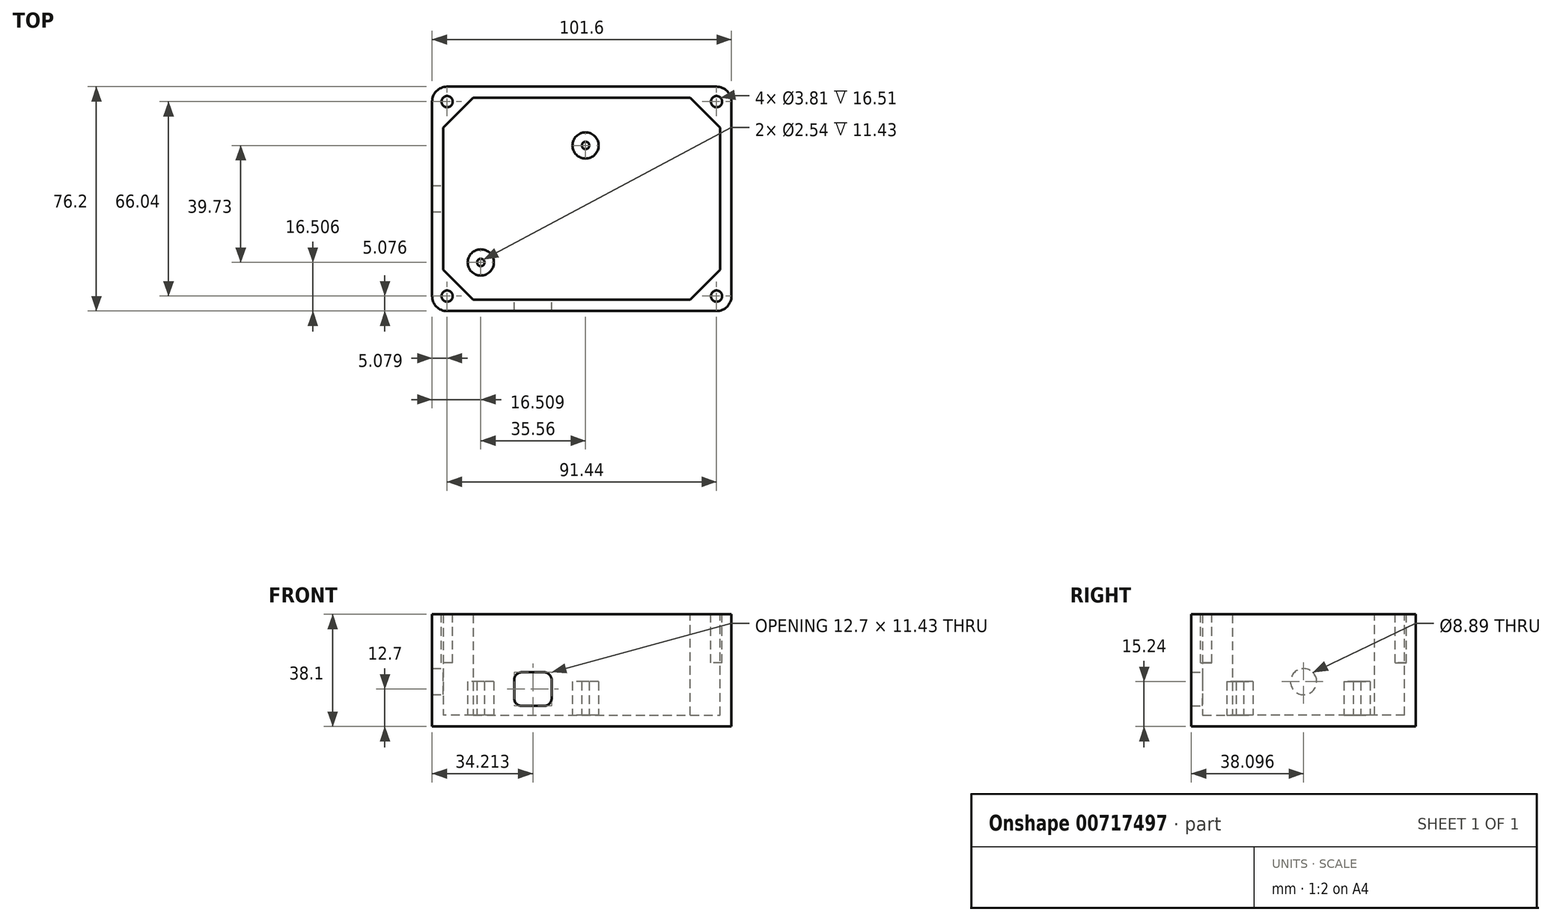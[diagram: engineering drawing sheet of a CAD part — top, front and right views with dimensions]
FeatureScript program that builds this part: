
annotation { "Feature Type Name" : "Feature", "Feature Type Description" : "" }
export const myFeature = defineFeature(function(context is Context, id is Id, definition is map)
    precondition{}
    {
        {
            var Q0;
            Q0=qCreatedBy(makeId("Top.planeOp"),FACE);
            var sketch = newSketch(context, id + "F0", { "sketchPlane" : qUnion([Q0])});
            skLineSegment(sketch, "E0.bottom", {"start": v(-48.85, 38.94) * mm, "end": v(52.75, 38.94) * mm});
            skLineSegment(sketch, "E0.top", {"start": v(-48.85, -37.26) * mm, "end": v(52.75, -37.26) * mm});
            skLineSegment(sketch, "E0.left", {"start": v(-48.85, 38.94) * mm, "end": v(-48.85, -37.26) * mm});
            skLineSegment(sketch, "E0.right", {"start": v(52.75, 38.94) * mm, "end": v(52.75, -37.26) * mm});
            skPoint(sketch, "E1.visualSharp", {"position": v(-48.85, 38.94) * mm});
            skLineSegment(sketch, "E1.filletArc", {"start": v(-48.85, 38.94) * mm, "end": v(-48.85, 38.94) * mm});
            skPoint(sketch, "E2.visualSharp", {"position": v(52.75, 38.94) * mm});
            skLineSegment(sketch, "E2.filletArc", {"start": v(52.75, 38.94) * mm, "end": v(52.75, 38.94) * mm});
            skPoint(sketch, "E3.visualSharp", {"position": v(52.75, -37.26) * mm});
            skLineSegment(sketch, "E3.filletArc", {"start": v(52.75, -37.26) * mm, "end": v(52.75, -37.26) * mm});
            skPoint(sketch, "E4.visualSharp", {"position": v(-48.85, -37.26) * mm});
            skLineSegment(sketch, "E4.filletArc", {"start": v(-48.85, -37.26) * mm, "end": v(-48.85, -37.26) * mm});
            skSolve(sketch);
        }
        {
            var Q0;
            Q0 = qSketchRegion(id + "F0", true);
            extrude(context, id + "F1", {"entities" : qUnion([Q0]), "depth" : 38.1 * mm, "offsetDistance" : 25.4 * mm});
        }
        {
            var Q0;
            Q0=makeQuery(id+"F1.opExtrude","CAP_FACE",FACE,{"disambiguationData":[OSD([sQuery(id+"F0.wireOp",EDGE,"E0.bottom"),sQuery(id+"F0.wireOp",EDGE,"E0.top"),sQuery(id+"F0.wireOp",EDGE,"E0.left"),sQuery(id+"F0.wireOp",EDGE,"E0.right")])],"isStart":false});
            shell(context, id + "F2", {"entities" : qUnion([Q0]), "thickness" : 3.8 * mm});
        }
        {
            var Q0;
            Q0=makeQuery(id+"F2.opShell","OFFSET_EDGE",EDGE,{"disambiguationData":[OSD([sQuery(id+"F0.wireOp",EDGE,"E0.bottom"),sQuery(id+"F0.wireOp",EDGE,"E0.left")])]});
            var Q1;
            Q1=makeQuery(id+"F2.opShell","OFFSET_EDGE",EDGE,{"disambiguationData":[OSD([sQuery(id+"F0.wireOp",EDGE,"E0.bottom"),sQuery(id+"F0.wireOp",EDGE,"E0.right")])]});
            var Q2;
            Q2=makeQuery(id+"F2.opShell","OFFSET_EDGE",EDGE,{"disambiguationData":[OSD([sQuery(id+"F0.wireOp",EDGE,"E0.top"),sQuery(id+"F0.wireOp",EDGE,"E0.right")])]});
            var Q3;
            Q3=makeQuery(id+"F2.opShell","OFFSET_EDGE",EDGE,{"disambiguationData":[OSD([sQuery(id+"F0.wireOp",EDGE,"E0.top"),sQuery(id+"F0.wireOp",EDGE,"E0.left")])]});
            chamfer(context, id + "F3", {"entities" : qUnion([Q0, Q1, Q2, Q3]), "width" : 10.16 * mm, "tangentPropagation" : true});
        }
        {
            var Q0;
            Q0=makeQuery(id+"F2.opShell","OFFSET_FACE",FACE,{"disambiguationData":[OSD([sQuery(id+"F0.wireOp",EDGE,"E0.bottom"),sQuery(id+"F0.wireOp",EDGE,"E0.top"),sQuery(id+"F0.wireOp",EDGE,"E0.left"),sQuery(id+"F0.wireOp",EDGE,"E0.right")])]});
            var sketch = newSketch(context, id + "F4", { "sketchPlane" : qUnion([Q0])});
            skCircle(sketch, "E5", {"center": v(-32.34, -20.75) * mm, "radius": 1.27 * mm});
            skCircle(sketch, "E6", {"center": v(-32.34, -20.75) * mm, "radius": 4.45 * mm});
            skCircle(sketch, "E7", {"center": v(3.22, 18.98) * mm, "radius": 1.27 * mm});
            skCircle(sketch, "E8", {"center": v(3.22, 18.98) * mm, "radius": 4.45 * mm});
            skSolve(sketch);
        }
        {
            var Q0;
            Q0=makeQuery(id+"F2.opShell","OFFSET_FACE",FACE,{"disambiguationData":[OSD([sQuery(id+"F0.wireOp",EDGE,"E0.left")])]});
            var sketch = newSketch(context, id + "F5", { "sketchPlane" : qUnion([Q0])});
            skCircle(sketch, "E9", {"center": v(0.84, 15.24) * mm, "radius": 4.45 * mm});
            skSolve(sketch);
        }
        {
            var Q0;
            Q0 = qSketchRegion(id + "F4", true);
            extrude(context, id + "F6", {"entities" : qUnion([Q0]), "operationType" : NewBodyOperationType.ADD, "depth" : 11.43 * mm, "offsetDistance" : 25.4 * mm});
        }
        {
            var Q0;
            Q0 = qSketchRegion(id + "F5", true);
            extrude(context, id + "F7", {"entities" : qUnion([Q0]), "operationType" : NewBodyOperationType.REMOVE, "endBound" : BoundingType.UP_TO_NEXT, "oppositeDirection" : true, "depth" : 25.4 * mm, "offsetDistance" : 25.4 * mm});
        }
        {
            var Q0;
            Q0=makeQuery(id+"F2.opShell","OFFSET_FACE",FACE,{"disambiguationData":[OSD([sQuery(id+"F0.wireOp",EDGE,"E0.top")])]});
            var sketch = newSketch(context, id + "F8", { "sketchPlane" : qUnion([Q0])});
            skLineSegment(sketch, "E10.bottom", {"start": v(8.29, 18.41) * mm, "end": v(20.99, 18.41) * mm});
            skLineSegment(sketch, "E10.top", {"start": v(8.29, 6.99) * mm, "end": v(20.99, 6.99) * mm});
            skLineSegment(sketch, "E10.left", {"start": v(8.29, 18.41) * mm, "end": v(8.29, 6.98) * mm});
            skLineSegment(sketch, "E10.right", {"start": v(20.99, 18.42) * mm, "end": v(20.99, 6.99) * mm});
            skPoint(sketch, "E11", {"position": v(14.64, 12.7) * mm});
            skPoint(sketch, "E11.positionSnap0", {"position": v(8.29, 12.7) * mm});
            skPoint(sketch, "E11.positionSnap1", {"position": v(14.64, 6.99) * mm});
            skSolve(sketch);
        }
        {
            var Q0;
            Q0 = qSketchRegion(id + "F8", true);
            extrude(context, id + "F9", {"entities" : qUnion([Q0]), "operationType" : NewBodyOperationType.REMOVE, "endBound" : BoundingType.UP_TO_NEXT, "oppositeDirection" : true, "depth" : 25.4 * mm, "offsetDistance" : 25.4 * mm});
        }
        {
            var Q0;
            Q0=makeQuery(id+"F9.boolean.opBoolean","COPY",EDGE,{"derivedFrom":makeQuery(id+"F9.opExtrude","SWEPT_EDGE",EDGE,{"disambiguationData":[OSD([sQuery(id+"F8.wireOp",EDGE,"E10.top"),sQuery(id+"F8.wireOp",EDGE,"E10.left")])]})});
            var Q1;
            Q1=makeQuery(id+"F9.boolean.opBoolean","COPY",EDGE,{"derivedFrom":makeQuery(id+"F9.opExtrude","SWEPT_EDGE",EDGE,{"disambiguationData":[OSD([sQuery(id+"F8.wireOp",EDGE,"E10.top"),sQuery(id+"F8.wireOp",EDGE,"E10.right")])]})});
            var Q2;
            Q2=makeQuery(id+"F9.boolean.opBoolean","COPY",EDGE,{"derivedFrom":makeQuery(id+"F9.opExtrude","SWEPT_EDGE",EDGE,{"disambiguationData":[OSD([sQuery(id+"F8.wireOp",EDGE,"E10.bottom"),sQuery(id+"F8.wireOp",EDGE,"E10.right")])]})});
            var Q3;
            Q3=makeQuery(id+"F9.boolean.opBoolean","COPY",EDGE,{"derivedFrom":makeQuery(id+"F9.opExtrude","SWEPT_EDGE",EDGE,{"disambiguationData":[OSD([sQuery(id+"F8.wireOp",EDGE,"E10.bottom"),sQuery(id+"F8.wireOp",EDGE,"E10.left")])]})});
            fillet(context, id + "F10", {"entities" : qUnion([Q0, Q1, Q2, Q3]), "radius" : 2.54 * mm, "tangentPropagation" : true, "allowEdgeOverflow" : false});
        }
        {
            var Q0;
            Q0=makeQuery(id+"F1.opExtrude","SWEPT_EDGE",EDGE,{"disambiguationData":[OSD([sQuery(id+"F0.wireOp",EDGE,"E0.top"),sQuery(id+"F0.wireOp",EDGE,"E0.left")])]});
            var Q1;
            Q1=makeQuery(id+"F1.opExtrude","SWEPT_EDGE",EDGE,{"disambiguationData":[OSD([sQuery(id+"F0.wireOp",EDGE,"E0.top"),sQuery(id+"F0.wireOp",EDGE,"E0.right")])]});
            var Q2;
            Q2=makeQuery(id+"F1.opExtrude","SWEPT_EDGE",EDGE,{"disambiguationData":[OSD([sQuery(id+"F0.wireOp",EDGE,"E0.bottom"),sQuery(id+"F0.wireOp",EDGE,"E0.right")])]});
            var Q3;
            Q3=makeQuery(id+"F1.opExtrude","SWEPT_EDGE",EDGE,{"disambiguationData":[OSD([sQuery(id+"F0.wireOp",EDGE,"E0.bottom"),sQuery(id+"F0.wireOp",EDGE,"E0.left")])]});
            fillet(context, id + "F11", {"entities" : qUnion([Q0, Q1, Q2, Q3]), "radius" : 5.08 * mm, "tangentPropagation" : true, "allowEdgeOverflow" : false});
        }
        {
            var Q0;
            Q0=makeQuery(id+"F1.opExtrude","CAP_FACE",FACE,{"disambiguationData":[OSD([sQuery(id+"F0.wireOp",EDGE,"E0.bottom"),sQuery(id+"F0.wireOp",EDGE,"E0.top"),sQuery(id+"F0.wireOp",EDGE,"E0.left"),sQuery(id+"F0.wireOp",EDGE,"E0.right")])],"isStart":false});
            var sketch = newSketch(context, id + "F12", { "sketchPlane" : qUnion([Q0])});
            skCircle(sketch, "E12", {"center": v(-43.77, 33.86) * mm, "radius": 1.9 * mm});
            skCircle(sketch, "E13.0.1.0", {"center": v(-43.77, -32.18) * mm, "radius": 1.9 * mm});
            skCircle(sketch, "E13.1.0.0", {"center": v(47.67, 33.86) * mm, "radius": 1.9 * mm});
            skCircle(sketch, "E13.1.1.0", {"center": v(47.67, -32.18) * mm, "radius": 1.9 * mm});
            skCircle(sketch, "E13.2.0.0", {"center": v(139.1, 33.86) * mm, "radius": 1.9 * mm});
            skCircle(sketch, "E13.2.1.0", {"center": v(139.1, -32.18) * mm, "radius": 1.9 * mm});
            skLineSegment(sketch, "E13.direction1", {"start": v(-43.77, 33.86) * mm, "end": v(47.67, 33.86) * mm, "construction": true});
            skLineSegment(sketch, "E13.direction2", {"start": v(-43.77, 33.86) * mm, "end": v(-43.77, -32.18) * mm, "construction": true});
            skSolve(sketch);
        }
        {
            var Q0;
            Q0 = qSketchRegion(id + "F12", true);
            extrude(context, id + "F13", {"entities" : qUnion([Q0]), "operationType" : NewBodyOperationType.REMOVE, "oppositeDirection" : true, "depth" : 16.5 * mm, "offsetDistance" : 25.4 * mm});
        }
    });
